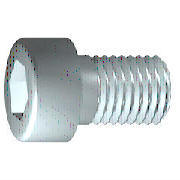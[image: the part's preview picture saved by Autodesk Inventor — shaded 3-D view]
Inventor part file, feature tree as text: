
AUTODESK INVENTOR PART (.ipt)
format: ipt  version: 2022 (Build 260153000, 153)  size: 196,096 bytes
history: native  units: mm (DEFAULTED — no unit token found)
features: sketch x2, other x1, extrude x1, plane x1, fillet x1
ambient origin geometry x7: Origin, YZ Plane, XY Plane, X Axis, Y Axis, Z Axis, Center Point
bodies: Solid1 (feature_tree)
feature tree (6):
  other  "Cuerpo"
  extrude  "Ranura"  Depth=4.0mm
  plane  "Work Plane1"
  fillet  "Fillet2"  Radius=4.0mm
  sketch  "Boceto1"  dims[d1=8.25mm d2=0.429515mm d3=4.0mm]
  sketch  "Boceto2"  dims[d4=2.0mm d5=60.0deg d6=4.0mm d7=4.0mm d8=3.464102mm d9=7.0mm d10=90.0deg d11=10.0mm d12=0.0mm d13=8.25mm d14=0.0mm d15=0.429415mm d16=0.429415mm d17=0.4mm d19=0.0mm d26=10.0mm d27=45.0deg d28=0.0mm d29=0.0mm d30=0.1mm]
